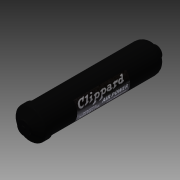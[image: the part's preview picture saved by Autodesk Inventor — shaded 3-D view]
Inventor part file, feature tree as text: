
AUTODESK INVENTOR PART (.ipt)
format: ipt  version: 2016 SP1 (Build 200210100, 210)  size: 187,392 bytes
history: native  units: in
note: dims shown in document units (in); Inventor stores cm internally (conversion verified against a paired STEP export)
features: sketch x8, extrude x4, revolve x3, fillet x2, other x2, projected_geometry x2, plane x1
ambient origin geometry x8: Origin, YZ Plane, XZ Plane, XY Plane, X Axis, Y Axis, Z Axis, Center Point
bodies: Solid1 (feature_tree)
feature tree (22):
  revolve  "Revolution1"  [1 undecoded]
  fillet  "Fillet1"  [1 undecoded]
  revolve  "Revolution2"  [1 undecoded]
  fillet  "Fillet2"  Radius=0.75in
  revolve  "Revolution3"  [1 undecoded]
  extrude  "Extrusion1"  Depth=0.144in TaperAngle=0.0deg
  extrude  "Extrusion2"  Depth=0.1in TaperAngle=0.0deg
  extrude  "Extrusion3"  [1 undecoded]
  extrude  "Extrusion4"  [1 undecoded]
  plane  "Work Plane1"
  other  "Decal1"
  sketch  "Sketch1"  dims[d0=1.28in d1=10.459in d2=90.0deg]
  sketch  "Sketch2"  dims[d3=0.75in d4=1.39in d5=0.75in]
  sketch  "Sketch3"  dims[d6=90.0deg d7=0.25in]
  sketch  "Sketch4"  dims[d8=90.0deg d9=0.144in d10=0.0in]
  projected_geometry  "Projected Loop1"
  sketch  "Sketch5"  dims[d11=0.322in d12=0.0in d13=0.1in d14=0.0in]
  projected_geometry  "Projected Loop2"
  sketch  "Sketch6"  dims[d15=0.1in d16=0.0in]
  sketch  "Sketch7"
  sketch  "Sketch8"
  other  "Image1"
note: 6 required parameter values undecoded (feature->parameter linkage not recoverable at this tier; creation-order binding heuristic only, values carry confidence <= 0.55)